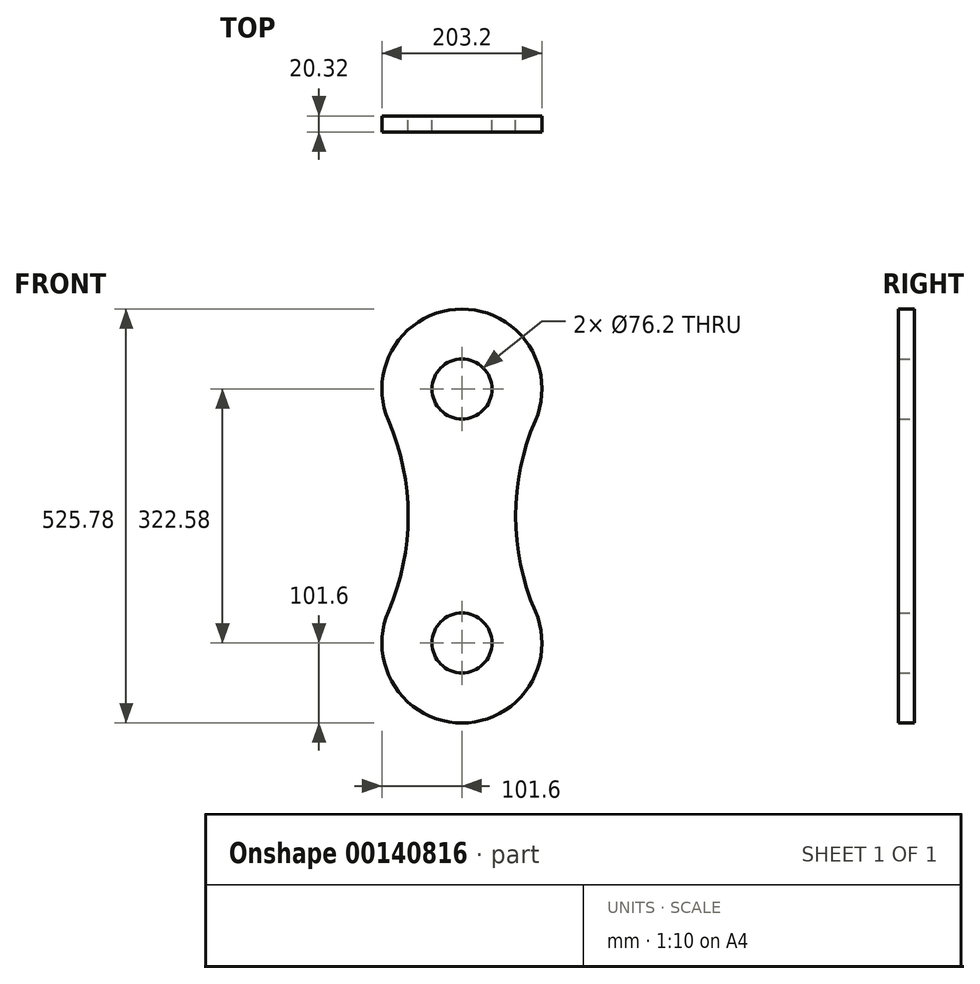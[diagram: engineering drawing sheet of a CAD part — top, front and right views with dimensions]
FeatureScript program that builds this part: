
annotation { "Feature Type Name" : "Feature", "Feature Type Description" : "" }
export const myFeature = defineFeature(function(context is Context, id is Id, definition is map)
    precondition{}
    {
        {
            var Q0;
            Q0=qCreatedBy(makeId("Front.planeOp"),FACE);
            var sketch = newSketch(context, id + "F0", { "sketchPlane" : qUnion([Q0])});
            skArc(sketch, "E0", {"start": v(93.29, 121.04) * mm, "mid": v(0, 262.9) * mm, "end": v(-93.29, 121.04) * mm});
            skArc(sketch, "E1", {"start": v(-93.29, -121.04) * mm, "mid": v(0, -262.9) * mm, "end": v(93.29, -121.04) * mm});
            skArc(sketch, "E2", {"start": v(-93.29, -121.04) * mm, "mid": v(-68.29, 0) * mm, "end": v(-93.29, 121.04) * mm});
            skArc(sketch, "E3.MirrorCS", {"start": v(93.29, -121.04) * mm, "mid": v(68.29, 0) * mm, "end": v(93.29, 121.04) * mm});
            skCircle(sketch, "E4", {"center": v(0, 161.3) * mm, "radius": 38.1 * mm});
            skCircle(sketch, "E5", {"center": v(0, -161.3) * mm, "radius": 38.1 * mm});
            skSolve(sketch);
        }
        {
            var Q0;
            Q0=makeQuery(id+"F0.imprint","IMPRINT",FACE,{"disambiguationData":[TD([[makeQuery(id+"F0.imprint","IMPRINT",EDGE,{"derivedFrom":sQuery(id+"F0.wireOp",EDGE,"E0")}),1.0]])]});
            extrude(context, id + "F1", {"entities" : qUnion([Q0]), "endBound" : BoundingType.SYMMETRIC, "depth" : 20.32 * mm});
        }
    });
